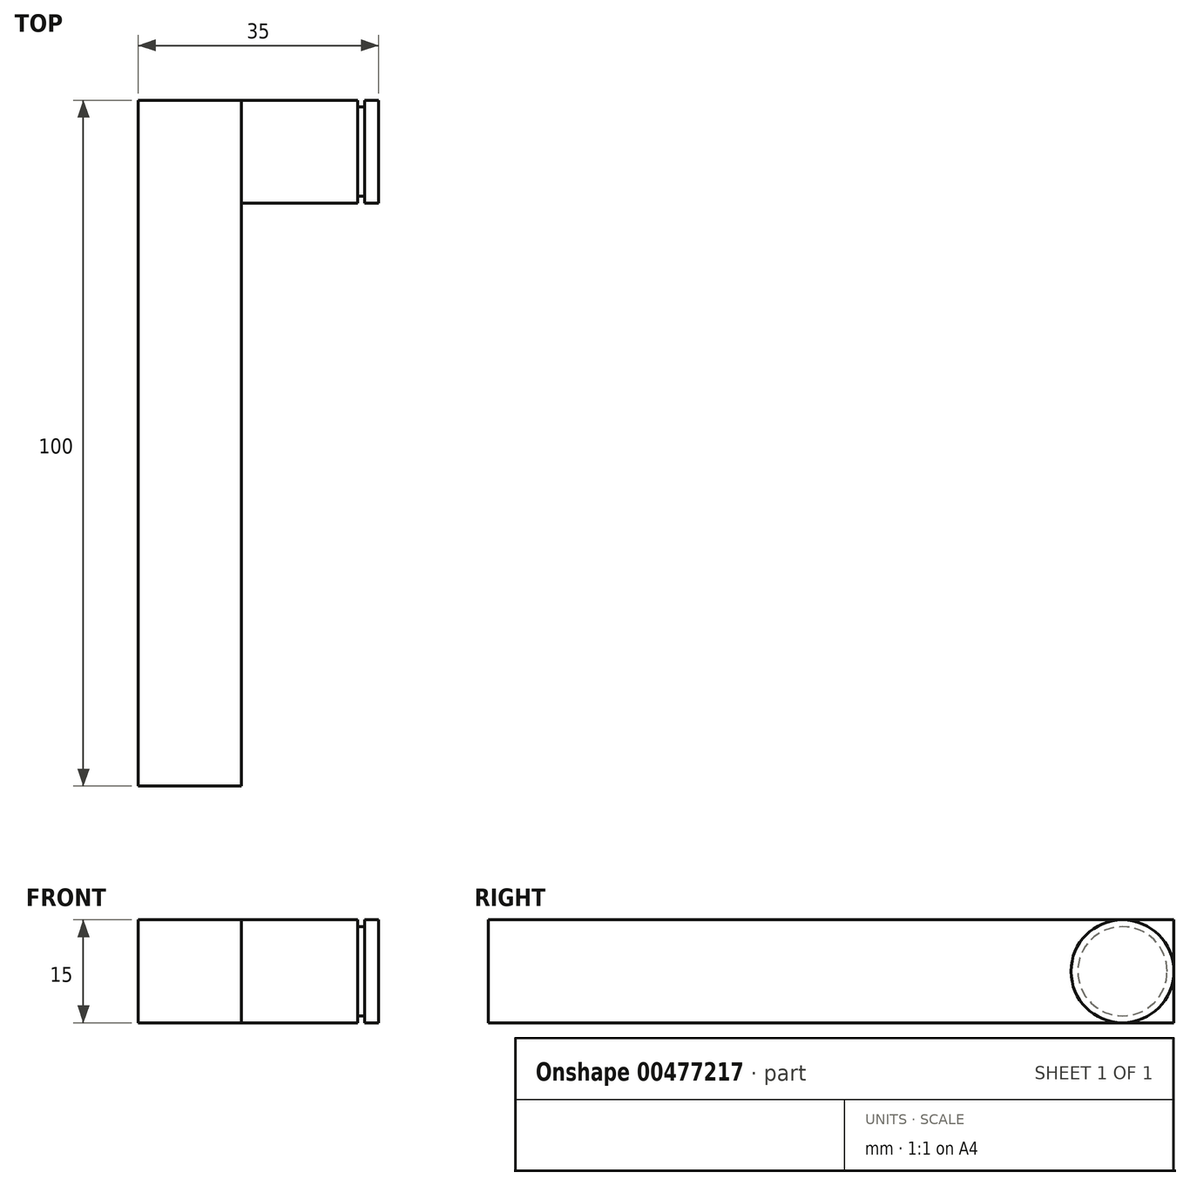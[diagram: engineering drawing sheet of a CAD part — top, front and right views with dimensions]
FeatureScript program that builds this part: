
annotation { "Feature Type Name" : "Feature", "Feature Type Description" : "" }
export const myFeature = defineFeature(function(context is Context, id is Id, definition is map)
    precondition{}
    {
        {
            var Q0;
            Q0=qCreatedBy(makeId("Top.planeOp"),FACE);
            var sketch = newSketch(context, id + "F0", { "sketchPlane" : qUnion([Q0])});
            skLineSegment(sketch, "E0.bottom", {"start": v(-15, -50) * mm, "end": v(0, -50) * mm});
            skLineSegment(sketch, "E0.top", {"start": v(-15, 50) * mm, "end": v(0, 50) * mm});
            skLineSegment(sketch, "E0.left", {"start": v(-15, -50) * mm, "end": v(-15, 50) * mm});
            skLineSegment(sketch, "E0.right", {"start": v(0, -50) * mm, "end": v(0, 50) * mm});
            skSolve(sketch);
        }
        {
            var Q0;
            Q0 = qSketchRegion(id + "F0", true);
            extrude(context, id + "F1", {"entities" : qUnion([Q0]), "endBound" : BoundingType.SYMMETRIC, "depth" : 15 * mm});
        }
        {
            var Q0;
            Q0=makeQuery(id+"F1.opExtrude","SWEPT_FACE",FACE,{"disambiguationData":[OSD([sQuery(id+"F0.wireOp",EDGE,"E0.right")])]});
            var sketch = newSketch(context, id + "F2", { "sketchPlane" : qUnion([Q0])});
            skCircle(sketch, "E1", {"center": v(42.5, 0) * mm, "radius": 7.5 * mm});
            skSolve(sketch);
        }
        {
            var Q0;
            Q0 = qSketchRegion(id + "F2", true);
            extrude(context, id + "F3", {"entities" : qUnion([Q0]), "operationType" : NewBodyOperationType.ADD, "depth" : 17 * mm});
        }
        {
            var Q0;
            Q0=makeQuery(id+"F3.opExtrude","CAP_FACE",FACE,{"disambiguationData":[OSD([sQuery(id+"F2.wireOp",EDGE,"E1")])],"isStart":false});
            var sketch = newSketch(context, id + "F4", { "sketchPlane" : qUnion([Q0])});
            skCircle(sketch, "E2", {"center": v(42.5, 0) * mm, "radius": 6.5 * mm});
            skSolve(sketch);
        }
        {
            var Q0;
            Q0 = qSketchRegion(id + "F4", true);
            extrude(context, id + "F5", {"entities" : qUnion([Q0]), "operationType" : NewBodyOperationType.ADD, "depth" : 1 * mm});
        }
        {
            var Q0;
            Q0=makeQuery(id+"F5.opExtrude","CAP_FACE",FACE,{"disambiguationData":[OSD([sQuery(id+"F4.wireOp",EDGE,"E2")])],"isStart":false});
            var sketch = newSketch(context, id + "F6", { "sketchPlane" : qUnion([Q0])});
            skCircle(sketch, "E3", {"center": v(42.5, 0) * mm, "radius": 7.5 * mm});
            skSolve(sketch);
        }
        {
            var Q0;
            Q0 = qSketchRegion(id + "F6", true);
            extrude(context, id + "F7", {"entities" : qUnion([Q0]), "operationType" : NewBodyOperationType.ADD, "depth" : 2 * mm});
        }
    });
